# Revit family: Accessory-Traps_Supplies_Stops-KOHLER-Awaken-K-98350
name_source: partatom
category: Plumbing Fixtures
revit_build: Autodesk Revit 2015 (Build: 20140606_1530(x64)
units: mm (PartAtom-declared; Revit-internal decimal feet)

## types (3) — shared parameters
ADA Compliant = Yes
Assembly Code = C1030200
Date Modified = 09/18/2017
Default Elevation = 42"
Description = Awaken Wall-mount Supply Elbow
HW Connection = Yes
Height = 2 5/16"
Length = 2 9/32"
Manufacturer = Kohler
MasterFormat 1995 = 10820
MasterFormat 2004 = 10.28.13
Material = Metal Construction
Product Documentation Link = http://www.us.kohler.com
Product Name = Awaken
Product Page URL = http://www.us.kohler.com
URL = http://www.us.kohler.com
Width = 2"

## per-type parameters (varying)
| type | Finish | Model | Type |
| CP-Polished Chrome | Kohler-Metal-CP-Polished_Chrome | K-98350-CP | 1 |
| BN-Vibrant Brushed Nickel | Kohler-Metal-BN-Vibrant_Brushed_Nickel | K-98350-BN | 2 |
| 2BZ-Oil Rubbed Bronze | Kohler-Metal-2BZ-Oil_Rubbed_Bronze | K-98350-2BZ | 3 |

## geometry (parser evidence)
native form markers: Blend x4, Sweep x5
no freeform markers — native parametric forms only
